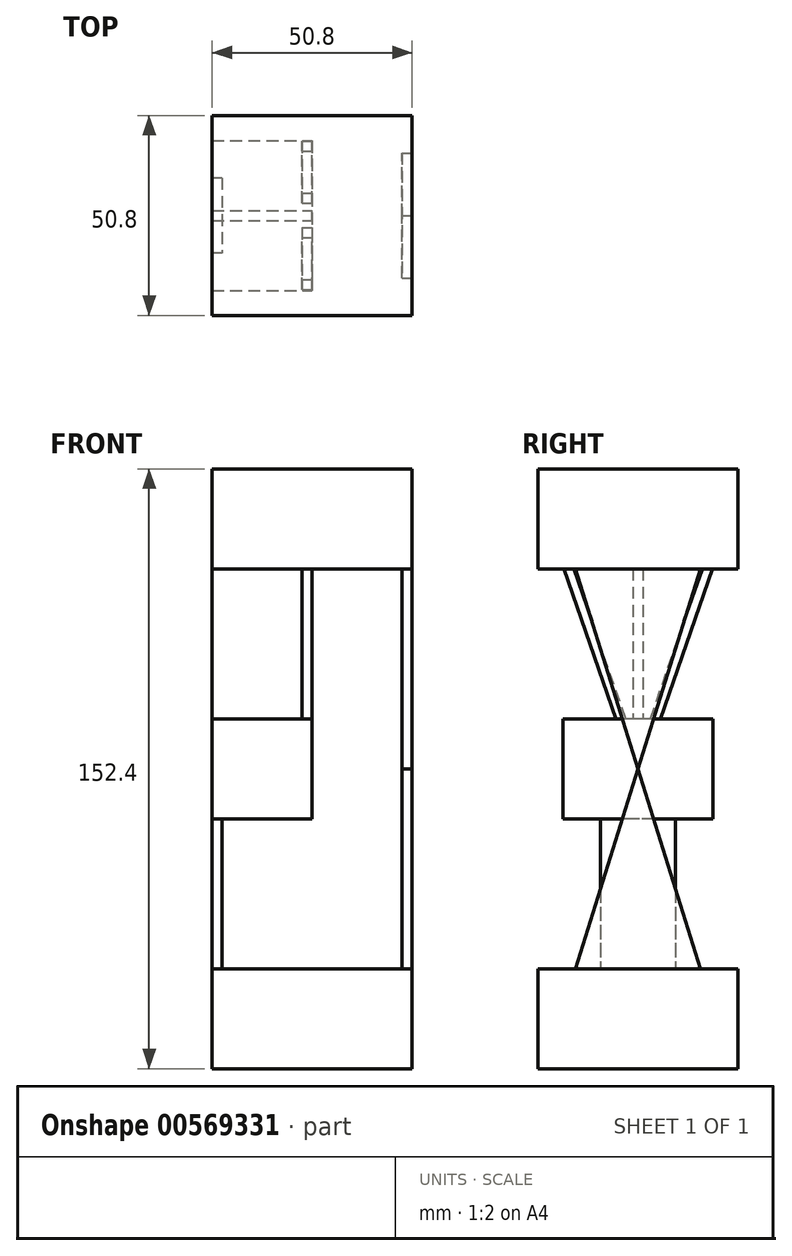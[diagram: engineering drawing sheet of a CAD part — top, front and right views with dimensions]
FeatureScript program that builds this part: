
annotation { "Feature Type Name" : "Feature", "Feature Type Description" : "" }
export const myFeature = defineFeature(function(context is Context, id is Id, definition is map)
    precondition{}
    {
        {
            var Q0;
            Q0=qCreatedBy(makeId("Top.planeOp"),FACE);
            var sketch = newSketch(context, id + "F0", { "sketchPlane" : qUnion([Q0])});
            skLineSegment(sketch, "E0.bottom", {"start": v(25.4, 25.4) * mm, "end": v(-25.4, 25.4) * mm});
            skLineSegment(sketch, "E0.top", {"start": v(25.4, -25.4) * mm, "end": v(-25.4, -25.4) * mm});
            skLineSegment(sketch, "E0.left", {"start": v(25.4, 25.4) * mm, "end": v(25.4, -25.4) * mm});
            skLineSegment(sketch, "E0.right", {"start": v(-25.4, 25.4) * mm, "end": v(-25.4, -25.4) * mm});
            skPoint(sketch, "E0.middle", {"position": v(0, 0) * mm});
            skSolve(sketch);
        }
        {
            var Q0;
            Q0 = qSketchRegion(id + "F0", true);
            extrude(context, id + "F1", {"entities" : qUnion([Q0]), "depth" : 25.4 * mm, "offsetDistance" : 25.4 * mm});
        }
        {
            var Q0;
            Q0=makeQuery(id+"F1.opExtrude","CAP_FACE",FACE,{"disambiguationData":[OSD([sQuery(id+"F0.wireOp",EDGE,"E0.bottom"),sQuery(id+"F0.wireOp",EDGE,"E0.top"),sQuery(id+"F0.wireOp",EDGE,"E0.left"),sQuery(id+"F0.wireOp",EDGE,"E0.right")])],"isStart":false});
            var sketch = newSketch(context, id + "F2", { "sketchPlane" : qUnion([Q0])});
            skLineSegment(sketch, "E1.bottom", {"start": v(-22.86, 9.52) * mm, "end": v(-25.4, 9.52) * mm});
            skLineSegment(sketch, "E1.top", {"start": v(-22.86, -9.53) * mm, "end": v(-25.4, -9.53) * mm});
            skLineSegment(sketch, "E1.left", {"start": v(-22.86, 9.53) * mm, "end": v(-22.86, -9.53) * mm});
            skLineSegment(sketch, "E1.right", {"start": v(-25.4, 9.53) * mm, "end": v(-25.4, -9.53) * mm});
            skPoint(sketch, "E2", {"position": v(-25.4, 0) * mm});
            skSolve(sketch);
        }
        {
            var Q0;
            Q0 = qSketchRegion(id + "F2", true);
            extrude(context, id + "F3", {"entities" : qUnion([Q0]), "operationType" : NewBodyOperationType.ADD, "depth" : 38.1 * mm, "offsetDistance" : 25.4 * mm});
        }
        {
            var Q0;
            Q0=makeQuery(id+"F3.opExtrude","CAP_FACE",FACE,{"disambiguationData":[OSD([sQuery(id+"F2.wireOp",EDGE,"E1.bottom"),sQuery(id+"F2.wireOp",EDGE,"E1.top"),sQuery(id+"F2.wireOp",EDGE,"E1.left"),sQuery(id+"F2.wireOp",EDGE,"E1.right")])],"isStart":false});
            var sketch = newSketch(context, id + "F4", { "sketchPlane" : qUnion([Q0])});
            skLineSegment(sketch, "E3.bottom", {"start": v(-25.4, 19.05) * mm, "end": v(0, 19.05) * mm});
            skLineSegment(sketch, "E3.top", {"start": v(-25.4, -19.05) * mm, "end": v(0, -19.05) * mm});
            skLineSegment(sketch, "E3.left", {"start": v(-25.4, 19.05) * mm, "end": v(-25.4, -19.05) * mm});
            skLineSegment(sketch, "E3.right", {"start": v(0, 19.05) * mm, "end": v(0, -19.05) * mm});
            skSolve(sketch);
        }
        {
            var Q0;
            Q0 = qSketchRegion(id + "F4", true);
            extrude(context, id + "F5", {"entities" : qUnion([Q0]), "operationType" : NewBodyOperationType.ADD, "depth" : 25.4 * mm, "offsetDistance" : 25.4 * mm});
        }
        {
            var Q0;
            Q0=makeQuery(id+"F5.opExtrude","SWEPT_FACE",FACE,{"disambiguationData":[OSD([sQuery(id+"F4.wireOp",EDGE,"E3.right")])]});
            var sketch = newSketch(context, id + "F6", { "sketchPlane" : qUnion([Q0])});
            skLineSegment(sketch, "E4.bottom", {"start": v(-1.27, 127) * mm, "end": v(1.27, 127) * mm});
            skLineSegment(sketch, "E4.top", {"start": v(-1.27, 88.9) * mm, "end": v(1.27, 88.9) * mm});
            skLineSegment(sketch, "E4.left", {"start": v(-1.27, 127) * mm, "end": v(-1.27, 88.9) * mm});
            skLineSegment(sketch, "E4.right", {"start": v(1.27, 127) * mm, "end": v(1.27, 88.9) * mm});
            skPoint(sketch, "E5", {"position": v(0, 88.9) * mm});
            skSolve(sketch);
        }
        {
            var Q0;
            Q0 = qSketchRegion(id + "F6", true);
            extrude(context, id + "F7", {"entities" : qUnion([Q0]), "oppositeDirection" : true, "depth" : 25.4 * mm, "offsetDistance" : 25.4 * mm});
        }
        {
            var Q0;
            Q0=makeQuery(id+"F5.opExtrude","SWEPT_FACE",FACE,{"disambiguationData":[OSD([sQuery(id+"F4.wireOp",EDGE,"E3.right")])]});
            var sketch = newSketch(context, id + "F8", { "sketchPlane" : qUnion([Q0])});
            skLineSegment(sketch, "E6", {"start": v(3.13, 88.9) * mm, "end": v(16.32, 127) * mm});
            skLineSegment(sketch, "E7", {"start": v(16.32, 127) * mm, "end": v(18.86, 127) * mm});
            skLineSegment(sketch, "E8", {"start": v(18.86, 127) * mm, "end": v(5.67, 88.9) * mm});
            skLineSegment(sketch, "E9", {"start": v(5.67, 88.9) * mm, "end": v(3.13, 88.9) * mm});
            skLineSegment(sketch, "E10", {"start": v(-3.13, 88.9) * mm, "end": v(-16.32, 127) * mm});
            skLineSegment(sketch, "E11", {"start": v(-16.32, 127) * mm, "end": v(-18.86, 127) * mm});
            skLineSegment(sketch, "E12", {"start": v(-18.86, 127) * mm, "end": v(-5.67, 88.9) * mm});
            skLineSegment(sketch, "E13", {"start": v(-5.67, 88.9) * mm, "end": v(-3.13, 88.9) * mm});
            skLineSegment(sketch, "E14", {"start": v(-19.05, 76.2) * mm, "end": v(19.05, 76.2) * mm, "construction": true});
            skLineSegment(sketch, "E15", {"start": v(0, 76.2) * mm, "end": v(4.4, 88.9) * mm, "construction": true});
            skLineSegment(sketch, "E16", {"start": v(0, 76.2) * mm, "end": v(-4.4, 88.9) * mm, "construction": true});
            skSolve(sketch);
        }
        {
            var Q0;
            Q0 = qSketchRegion(id + "F8", true);
            extrude(context, id + "F9", {"entities" : qUnion([Q0]), "oppositeDirection" : true, "depth" : 2.54 * mm, "offsetDistance" : 25.4 * mm});
        }
        {
            var Q0;
            Q0=makeQuery(id+"F7.opExtrude","SWEPT_FACE",FACE,{"disambiguationData":[OSD([sQuery(id+"F6.wireOp",EDGE,"E4.bottom")])]});
            var sketch = newSketch(context, id + "F10", { "sketchPlane" : qUnion([Q0])});
            skLineSegment(sketch, "E17.bottom", {"start": v(25.4, 25.4) * mm, "end": v(-25.4, 25.4) * mm});
            skLineSegment(sketch, "E17.top", {"start": v(25.4, -25.4) * mm, "end": v(-25.4, -25.4) * mm});
            skLineSegment(sketch, "E17.left", {"start": v(25.4, 25.4) * mm, "end": v(25.4, -25.4) * mm});
            skLineSegment(sketch, "E17.right", {"start": v(-25.4, 25.4) * mm, "end": v(-25.4, -25.4) * mm});
            skPoint(sketch, "E17.middle", {"position": v(0, 0) * mm});
            skSolve(sketch);
        }
        {
            var Q0;
            Q0 = qSketchRegion(id + "F10", true);
            extrude(context, id + "F11", {"entities" : qUnion([Q0]), "depth" : 25.4 * mm, "offsetDistance" : 25.4 * mm});
        }
        {
            var Q0;
            Q0=makeQuery(id+"F1.opExtrude","SWEPT_FACE",FACE,{"disambiguationData":[OSD([sQuery(id+"F0.wireOp",EDGE,"E0.left")])]});
            var sketch = newSketch(context, id + "F12", { "sketchPlane" : qUnion([Q0])});
            skLineSegment(sketch, "E18", {"start": v(-15.87, 25.4) * mm, "end": v(15.88, 127) * mm});
            skLineSegment(sketch, "E19", {"start": v(15.88, 127) * mm, "end": v(-15.88, 127) * mm});
            skLineSegment(sketch, "E20", {"start": v(-15.88, 127) * mm, "end": v(15.87, 25.4) * mm});
            skLineSegment(sketch, "E21", {"start": v(15.87, 25.4) * mm, "end": v(-15.87, 25.4) * mm});
            skLineSegment(sketch, "E22", {"start": v(15.87, 127) * mm, "end": v(15.88, 25.4) * mm, "construction": true});
            skLineSegment(sketch, "E23", {"start": v(-15.88, 127) * mm, "end": v(-15.87, 25.4) * mm, "construction": true});
            skPoint(sketch, "E24", {"position": v(0, 25.4) * mm});
            skPoint(sketch, "E25", {"position": v(0, 127) * mm});
            skSolve(sketch);
        }
        {
            var Q0;
            Q0 = qSketchRegion(id + "F12", true);
            extrude(context, id + "F13", {"entities" : qUnion([Q0]), "oppositeDirection" : true, "depth" : 2.54 * mm, "offsetDistance" : 25.4 * mm});
        }
    });
